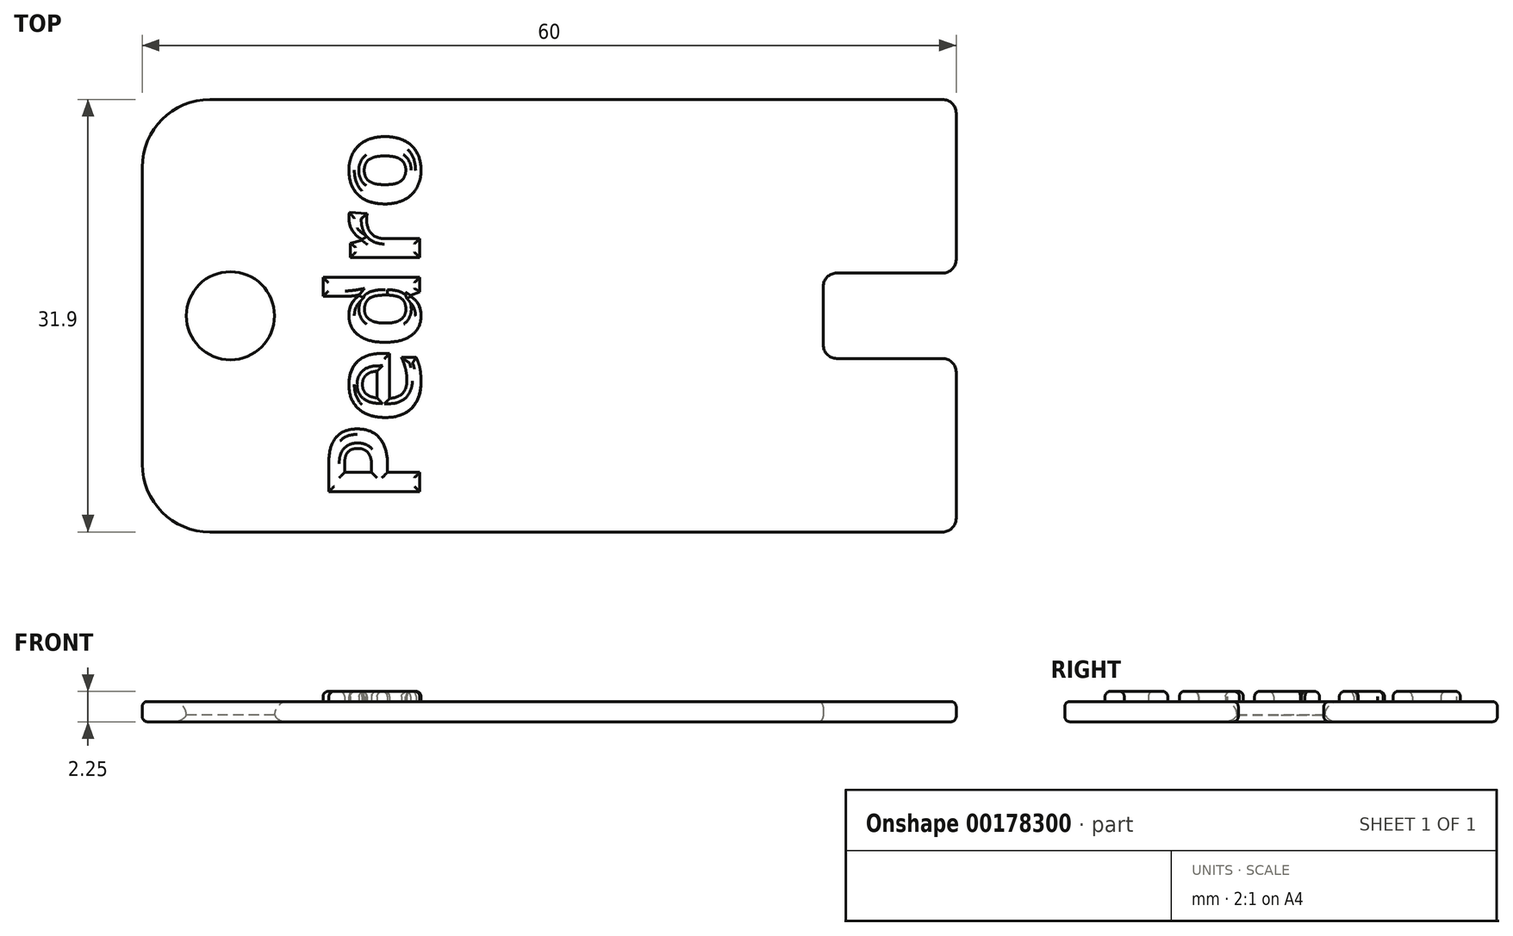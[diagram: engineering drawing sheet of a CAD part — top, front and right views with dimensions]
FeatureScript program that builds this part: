
annotation { "Feature Type Name" : "Feature", "Feature Type Description" : "" }
export const myFeature = defineFeature(function(context is Context, id is Id, definition is map)
    precondition{}
    {
        {
            var Q0;
            Q0=qCreatedBy(makeId("Top.planeOp"),FACE);
            var sketch = newSketch(context, id + "F0", { "sketchPlane" : qUnion([Q0])});
            skLineSegment(sketch, "E0.bottom", {"start": v(-5.98, -13.53) * mm, "end": v(48.02, -13.53) * mm});
            skLineSegment(sketch, "E0.top", {"start": v(-5.98, -45.43) * mm, "end": v(48.02, -45.43) * mm});
            skLineSegment(sketch, "E0.left", {"start": v(-10.98, -18.53) * mm, "end": v(-10.98, -40.43) * mm});
            skLineSegment(sketch, "E0.right", {"start": v(49.02, -14.53) * mm, "end": v(49.02, -25.33) * mm});
            skPoint(sketch, "E1", {"position": v(-4.48, -29.48) * mm});
            skPoint(sketch, "E1.positionSnap0", {"position": v(-10.98, -29.48) * mm});
            skLineSegment(sketch, "E2.bottom", {"start": v(48.02, -26.33) * mm, "end": v(40.22, -26.33) * mm});
            skLineSegment(sketch, "E2.top", {"start": v(48.02, -32.63) * mm, "end": v(40.22, -32.63) * mm});
            skLineSegment(sketch, "E2.right", {"start": v(39.22, -27.33) * mm, "end": v(39.22, -31.63) * mm});
            skLineSegment(sketch, "E3.trimOffspring", {"start": v(49.02, -33.63) * mm, "end": v(49.02, -44.43) * mm});
            skCircle(sketch, "E4", {"center": v(-4.48, -29.48) * mm, "radius": 3.25 * mm});
            skPoint(sketch, "E5.visualSharp", {"position": v(49.02, -13.53) * mm});
            skArc(sketch, "E5.filletArc", {"start": v(49.02, -14.53) * mm, "mid": v(48.73, -13.82) * mm, "end": v(48.02, -13.53) * mm});
            skPoint(sketch, "E6.visualSharp", {"position": v(49.02, -45.43) * mm});
            skArc(sketch, "E6.filletArc", {"start": v(48.02, -45.43) * mm, "mid": v(48.73, -45.14) * mm, "end": v(49.02, -44.43) * mm});
            skPoint(sketch, "E7.visualSharp", {"position": v(49.02, -32.63) * mm});
            skArc(sketch, "E7.filletArc", {"start": v(49.02, -33.63) * mm, "mid": v(48.73, -32.92) * mm, "end": v(48.02, -32.63) * mm});
            skPoint(sketch, "E8.visualSharp", {"position": v(49.02, -26.33) * mm});
            skArc(sketch, "E8.filletArc", {"start": v(48.02, -26.33) * mm, "mid": v(48.73, -26.04) * mm, "end": v(49.02, -25.33) * mm});
            skPoint(sketch, "E9.visualSharp", {"position": v(39.22, -26.33) * mm});
            skArc(sketch, "E9.filletArc", {"start": v(40.22, -26.33) * mm, "mid": v(39.52, -26.62) * mm, "end": v(39.22, -27.33) * mm});
            skPoint(sketch, "E10.visualSharp", {"position": v(39.22, -32.63) * mm});
            skArc(sketch, "E10.filletArc", {"start": v(39.22, -31.63) * mm, "mid": v(39.52, -32.34) * mm, "end": v(40.22, -32.63) * mm});
            skPoint(sketch, "E11.visualSharp", {"position": v(-10.98, -13.53) * mm});
            skArc(sketch, "E11.filletArc", {"start": v(-5.98, -13.53) * mm, "mid": v(-9.51, -15) * mm, "end": v(-10.98, -18.53) * mm});
            skPoint(sketch, "E12.visualSharp", {"position": v(-10.98, -45.43) * mm});
            skArc(sketch, "E12.filletArc", {"start": v(-10.98, -40.43) * mm, "mid": v(-9.51, -43.96) * mm, "end": v(-5.98, -45.43) * mm});
            skSolve(sketch);
        }
        {
            var Q0;
            Q0=makeQuery(id+"F0.imprint","IMPRINT",FACE,{"disambiguationData":[TD([[makeQuery(id+"F0.imprint","IMPRINT",EDGE,{"derivedFrom":sQuery(id+"F0.wireOp",EDGE,"E0.bottom")}),-1.0]])]});
            extrude(context, id + "F1", {"entities" : qUnion([Q0]), "depth" : 1.5 * mm});
        }
        {
            var Q0;
            Q0=makeQuery(id+"F1.opExtrude","CAP_FACE",FACE,{"disambiguationData":[OSD([sQuery(id+"F0.wireOp",EDGE,"E0.bottom"),sQuery(id+"F0.wireOp",EDGE,"E0.top"),sQuery(id+"F0.wireOp",EDGE,"E0.left"),sQuery(id+"F0.wireOp",EDGE,"E0.right"),sQuery(id+"F0.wireOp",EDGE,"E2.bottom"),sQuery(id+"F0.wireOp",EDGE,"E2.top"),sQuery(id+"F0.wireOp",EDGE,"E2.right"),sQuery(id+"F0.wireOp",EDGE,"E3.trimOffspring"),sQuery(id+"F0.wireOp",EDGE,"E4"),sQuery(id+"F0.wireOp",EDGE,"E5.filletArc"),sQuery(id+"F0.wireOp",EDGE,"E6.filletArc"),sQuery(id+"F0.wireOp",EDGE,"E7.filletArc"),sQuery(id+"F0.wireOp",EDGE,"E8.filletArc"),sQuery(id+"F0.wireOp",EDGE,"E9.filletArc"),sQuery(id+"F0.wireOp",EDGE,"E10.filletArc"),sQuery(id+"F0.wireOp",EDGE,"E11.filletArc"),sQuery(id+"F0.wireOp",EDGE,"E12.filletArc")])],"isStart":false});
            var sketch = newSketch(context, id + "F2", { "sketchPlane" : qUnion([Q0])});
            skText(sketch, "E13", { "text": "Pedro", "fontName": "OpenSans-Bold.ttf"});
            const initialGuessF2  = {"E13": [0.00948, -0.0433, 0, 1, 0.00676]};
            skSetInitialGuess(sketch, initialGuessF2);
            skSolve(sketch);
        }
        {
            var Q0;
            Q0 = qSketchRegion(id + "F2", true);
            extrude(context, id + "F3", {"entities" : qUnion([Q0]), "operationType" : NewBodyOperationType.ADD, "depth" : 0.75 * mm});
        }
        {
            var Q0;
            Q0=makeQuery(id+"F1.opExtrude","CAP_EDGE",EDGE,{"disambiguationData":[OSD([sQuery(id+"F0.wireOp",EDGE,"E4")])],"isStart":false});
            fillet(context, id + "F4", {"entities" : qUnion([Q0]), "radius" : 1 * mm, "tangentPropagation" : true, "allowEdgeOverflow" : false});
        }
        {
            var Q0;
            Q0=makeQuery(id+"F3.opExtrude","CAP_FACE",FACE,{"disambiguationData":[OSD([sQuery(id+"F2.wireOp",EDGE,"E13.sketch_text.stroke-72"),sQuery(id+"F2.wireOp",EDGE,"E13.sketch_text.stroke-73"),sQuery(id+"F2.wireOp",EDGE,"E13.sketch_text.stroke-74"),sQuery(id+"F2.wireOp",EDGE,"E13.sketch_text.stroke-75"),sQuery(id+"F2.wireOp",EDGE,"E13.sketch_text.stroke-76"),sQuery(id+"F2.wireOp",EDGE,"E13.sketch_text.stroke-77"),sQuery(id+"F2.wireOp",EDGE,"E13.sketch_text.stroke-78"),sQuery(id+"F2.wireOp",EDGE,"E13.sketch_text.stroke-79"),sQuery(id+"F2.wireOp",EDGE,"E13.sketch_text.stroke-80"),sQuery(id+"F2.wireOp",EDGE,"E13.sketch_text.stroke-81"),sQuery(id+"F2.wireOp",EDGE,"E13.sketch_text.stroke-82"),sQuery(id+"F2.wireOp",EDGE,"E13.sketch_text.stroke-83"),sQuery(id+"F2.wireOp",EDGE,"E13.sketch_text.stroke-84"),sQuery(id+"F2.wireOp",EDGE,"E13.sketch_text.stroke-85"),sQuery(id+"F2.wireOp",EDGE,"E13.sketch_text.stroke-86"),sQuery(id+"F2.wireOp",EDGE,"E13.sketch_text.stroke-87"),sQuery(id+"F2.wireOp",EDGE,"E13.sketch_text.stroke-88"),sQuery(id+"F2.wireOp",EDGE,"E13.sketch_text.stroke-89")])],"isStart":false});
            var Q1;
            Q1=makeQuery(id+"F3.opExtrude","CAP_FACE",FACE,{"disambiguationData":[OSD([sQuery(id+"F2.wireOp",EDGE,"E13.sketch_text.stroke-59"),sQuery(id+"F2.wireOp",EDGE,"E13.sketch_text.stroke-60"),sQuery(id+"F2.wireOp",EDGE,"E13.sketch_text.stroke-61"),sQuery(id+"F2.wireOp",EDGE,"E13.sketch_text.stroke-62"),sQuery(id+"F2.wireOp",EDGE,"E13.sketch_text.stroke-63"),sQuery(id+"F2.wireOp",EDGE,"E13.sketch_text.stroke-64"),sQuery(id+"F2.wireOp",EDGE,"E13.sketch_text.stroke-65"),sQuery(id+"F2.wireOp",EDGE,"E13.sketch_text.stroke-66"),sQuery(id+"F2.wireOp",EDGE,"E13.sketch_text.stroke-67"),sQuery(id+"F2.wireOp",EDGE,"E13.sketch_text.stroke-68"),sQuery(id+"F2.wireOp",EDGE,"E13.sketch_text.stroke-69"),sQuery(id+"F2.wireOp",EDGE,"E13.sketch_text.stroke-70"),sQuery(id+"F2.wireOp",EDGE,"E13.sketch_text.stroke-71")])],"isStart":false});
            var Q2;
            Q2=makeQuery(id+"F3.opExtrude","CAP_FACE",FACE,{"disambiguationData":[OSD([sQuery(id+"F2.wireOp",EDGE,"E13.sketch_text.stroke-36"),sQuery(id+"F2.wireOp",EDGE,"E13.sketch_text.stroke-37"),sQuery(id+"F2.wireOp",EDGE,"E13.sketch_text.stroke-38"),sQuery(id+"F2.wireOp",EDGE,"E13.sketch_text.stroke-39"),sQuery(id+"F2.wireOp",EDGE,"E13.sketch_text.stroke-40"),sQuery(id+"F2.wireOp",EDGE,"E13.sketch_text.stroke-41"),sQuery(id+"F2.wireOp",EDGE,"E13.sketch_text.stroke-42"),sQuery(id+"F2.wireOp",EDGE,"E13.sketch_text.stroke-43"),sQuery(id+"F2.wireOp",EDGE,"E13.sketch_text.stroke-44"),sQuery(id+"F2.wireOp",EDGE,"E13.sketch_text.stroke-45"),sQuery(id+"F2.wireOp",EDGE,"E13.sketch_text.stroke-46"),sQuery(id+"F2.wireOp",EDGE,"E13.sketch_text.stroke-47"),sQuery(id+"F2.wireOp",EDGE,"E13.sketch_text.stroke-48"),sQuery(id+"F2.wireOp",EDGE,"E13.sketch_text.stroke-49"),sQuery(id+"F2.wireOp",EDGE,"E13.sketch_text.stroke-50"),sQuery(id+"F2.wireOp",EDGE,"E13.sketch_text.stroke-51"),sQuery(id+"F2.wireOp",EDGE,"E13.sketch_text.stroke-52"),sQuery(id+"F2.wireOp",EDGE,"E13.sketch_text.stroke-53"),sQuery(id+"F2.wireOp",EDGE,"E13.sketch_text.stroke-54"),sQuery(id+"F2.wireOp",EDGE,"E13.sketch_text.stroke-55"),sQuery(id+"F2.wireOp",EDGE,"E13.sketch_text.stroke-56"),sQuery(id+"F2.wireOp",EDGE,"E13.sketch_text.stroke-57"),sQuery(id+"F2.wireOp",EDGE,"E13.sketch_text.stroke-58")])],"isStart":false});
            var Q3;
            Q3=makeQuery(id+"F3.opExtrude","CAP_FACE",FACE,{"disambiguationData":[OSD([sQuery(id+"F2.wireOp",EDGE,"E13.sketch_text.stroke-16"),sQuery(id+"F2.wireOp",EDGE,"E13.sketch_text.stroke-17"),sQuery(id+"F2.wireOp",EDGE,"E13.sketch_text.stroke-18"),sQuery(id+"F2.wireOp",EDGE,"E13.sketch_text.stroke-19"),sQuery(id+"F2.wireOp",EDGE,"E13.sketch_text.stroke-20"),sQuery(id+"F2.wireOp",EDGE,"E13.sketch_text.stroke-21"),sQuery(id+"F2.wireOp",EDGE,"E13.sketch_text.stroke-22"),sQuery(id+"F2.wireOp",EDGE,"E13.sketch_text.stroke-23"),sQuery(id+"F2.wireOp",EDGE,"E13.sketch_text.stroke-24"),sQuery(id+"F2.wireOp",EDGE,"E13.sketch_text.stroke-25"),sQuery(id+"F2.wireOp",EDGE,"E13.sketch_text.stroke-26"),sQuery(id+"F2.wireOp",EDGE,"E13.sketch_text.stroke-27"),sQuery(id+"F2.wireOp",EDGE,"E13.sketch_text.stroke-28"),sQuery(id+"F2.wireOp",EDGE,"E13.sketch_text.stroke-29"),sQuery(id+"F2.wireOp",EDGE,"E13.sketch_text.stroke-30"),sQuery(id+"F2.wireOp",EDGE,"E13.sketch_text.stroke-31"),sQuery(id+"F2.wireOp",EDGE,"E13.sketch_text.stroke-32"),sQuery(id+"F2.wireOp",EDGE,"E13.sketch_text.stroke-33"),sQuery(id+"F2.wireOp",EDGE,"E13.sketch_text.stroke-34"),sQuery(id+"F2.wireOp",EDGE,"E13.sketch_text.stroke-35")])],"isStart":false});
            var Q4;
            Q4=makeQuery(id+"F3.opExtrude","CAP_FACE",FACE,{"disambiguationData":[OSD([sQuery(id+"F2.wireOp",EDGE,"E13.sketch_text.stroke-0"),sQuery(id+"F2.wireOp",EDGE,"E13.sketch_text.stroke-1"),sQuery(id+"F2.wireOp",EDGE,"E13.sketch_text.stroke-2"),sQuery(id+"F2.wireOp",EDGE,"E13.sketch_text.stroke-3"),sQuery(id+"F2.wireOp",EDGE,"E13.sketch_text.stroke-4"),sQuery(id+"F2.wireOp",EDGE,"E13.sketch_text.stroke-5"),sQuery(id+"F2.wireOp",EDGE,"E13.sketch_text.stroke-6"),sQuery(id+"F2.wireOp",EDGE,"E13.sketch_text.stroke-7"),sQuery(id+"F2.wireOp",EDGE,"E13.sketch_text.stroke-8"),sQuery(id+"F2.wireOp",EDGE,"E13.sketch_text.stroke-9"),sQuery(id+"F2.wireOp",EDGE,"E13.sketch_text.stroke-10"),sQuery(id+"F2.wireOp",EDGE,"E13.sketch_text.stroke-11"),sQuery(id+"F2.wireOp",EDGE,"E13.sketch_text.stroke-12"),sQuery(id+"F2.wireOp",EDGE,"E13.sketch_text.stroke-13"),sQuery(id+"F2.wireOp",EDGE,"E13.sketch_text.stroke-14"),sQuery(id+"F2.wireOp",EDGE,"E13.sketch_text.stroke-15")])],"isStart":false});
            fillet(context, id + "F5", {"entities" : qUnion([Q0, Q1, Q2, Q3, Q4]), "radius" : 0.4 * mm, "tangentPropagation" : true, "allowEdgeOverflow" : false});
        }
        {
            var Q0;
            Q0=makeQuery(id+"F1.opExtrude","CAP_EDGE",EDGE,{"disambiguationData":[OSD([sQuery(id+"F0.wireOp",EDGE,"E4")])],"isStart":true});
            fillet(context, id + "F6", {"entities" : qUnion([Q0]), "radius" : 1 * mm, "tangentPropagation" : true, "allowEdgeOverflow" : false});
        }
        {
            var Q0;
            Q0=makeQuery(id+"F1.opExtrude","SWEPT_FACE",FACE,{"disambiguationData":[OSD([sQuery(id+"F0.wireOp",EDGE,"E0.bottom")])]});
            fillet(context, id + "F7", {"entities" : qUnion([Q0]), "radius" : 0.4 * mm, "tangentPropagation" : true, "allowEdgeOverflow" : false});
        }
    });
